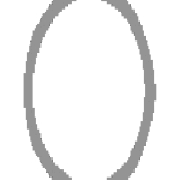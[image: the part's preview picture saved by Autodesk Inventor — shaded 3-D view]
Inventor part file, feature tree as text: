
AUTODESK INVENTOR PART (.ipt)
format: ipt  version: 2021 (Build 250183000, 183)  size: 115,200 bytes
history: native  units: in
note: dims shown in document units (in); Inventor stores cm internally (conversion verified against a paired STEP export)
features: other x4, sketch x3, plane x1
ambient origin geometry x8: Origin, YZ Plane, XZ Plane, XY Plane, X Axis, Y Axis, Z Axis, Center Point
bodies: Solid1 (feature_tree), Body (feature_tree)
feature tree (8):
  other  "Driven Length"
  other  "Frame Generator"
  other  "Start Plane"
  other  "End Plane"
  sketch  "Sketch"  dims[d2=4.559in d4=-0.0in d5=4.559in d6=0.12in d7=0.0in d8=90.0deg d9=4.559in]
  sketch  "Sketch2"  dims[d0=1.0in]
  plane  "Work Plane3"
  sketch  "Sketch3"  dims[d1=0.065in]
